# Revit family: Security_Bosch_Detectors_TriTech_ProSeries
name_source: partatom
category: Sicherheitsgeräte
revit_build: Autodesk Revit 2017 (Build: 20160225_1515(x64)
units: mm (PartAtom-declared; Revit-internal decimal feet)

## family parameters
Basisbauteil = Fläche
Beim Laden mit Abzugskörper schneiden = Nein
Bemaßung runder Anschluss = Durchmesser verwenden
Beschriftungsausrichtung beibehalten = Nein
Gemeinsam genutzt = Nein
OmniClass-Nummer = 23.85.30.14
OmniClass-Titel = Presence Detection/Registration
Raumberechnungspunkt = Nein
Teiletyp = Normal

## types (2) — shared parameters
Baugruppenkennzeichen = E1010
BodyMaterial = Xtech_Bosch_ABS_White
Depth = 44 mm  [stored 0.144357 ft]
Disclaimer = http://resource.boschsecurity.com
Height = 105 mm  [stored 0.344488 ft]
IfcExportAs = IfcElectricAppliance
IfcExportType = UNDEFINED
InstallationManual = http://resource.boschsecurity.us
ManufacturerURL = www.boschsecurity.com
Material = High Impact ABS plastic
ModelNumber = F.01U.025.758
ProductInformation = http://resource.boschsecurity.us
RevitCategory = SecurityDevices
Uniclass2015 = Ss_75_40_75_40:IntruderDetectionAndAlarmSystems
Version = 1
Width = 61 mm  [stored 0.200131 ft]
zero-valued in all types: Kosten, Vorgabe-Ansicht

## per-type parameters (varying)
| type | Beschreibung | ISC-PDL1-W18G | ISC-PDL1-W18H |
| ISC-PDL1-W18G, TriTech+ motion detector, 18m (60 ft) | Provides PIR and microwave, 18 m x 25 m (60 ft x 80 ft) coverage. 10.525 GHz frequency. | Ja | Nein |
| ISC-PDL1-W18H, TriTech+ motion detector, 18m (60 ft) | Provides PIR and microwave, 18 m x 25 m (60 ft x 80 ft) coverage. 10.588 GHz frequency. For use in France and United Kingdom. | Nein | Ja |

note: [stored X ft] marks values corroborated as IEEE doubles in the binary element streams (Revit-internal decimal feet)

## geometry (parser evidence)
native form markers: Sweep x5
no freeform markers — native parametric forms only
